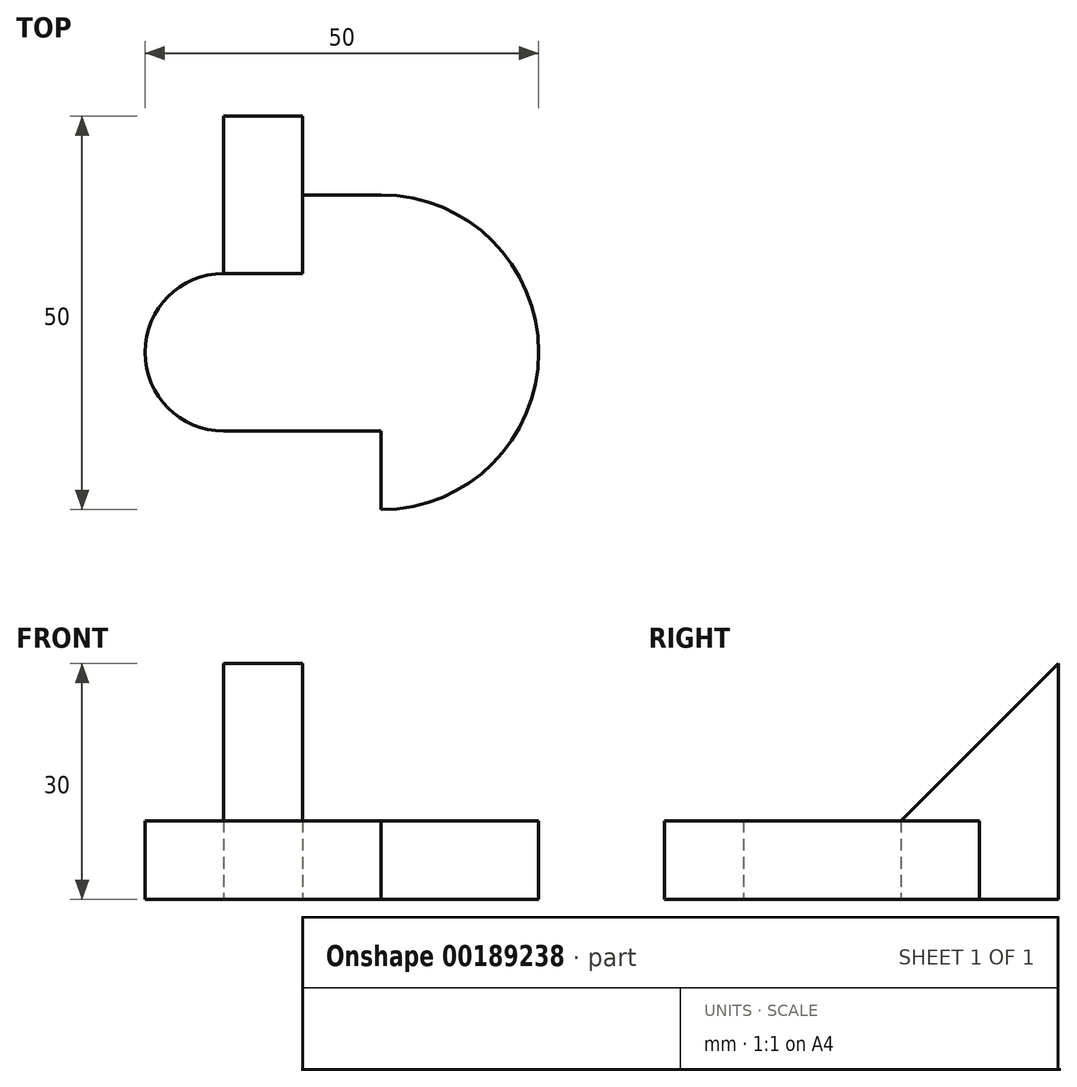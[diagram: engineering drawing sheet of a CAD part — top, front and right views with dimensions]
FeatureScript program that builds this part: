
annotation { "Feature Type Name" : "Feature", "Feature Type Description" : "" }
export const myFeature = defineFeature(function(context is Context, id is Id, definition is map)
    precondition{}
    {
        {
            var Q0;
            Q0=qCreatedBy(makeId("Top.planeOp"),FACE);
            var sketch = newSketch(context, id + "F0", { "sketchPlane" : qUnion([Q0])});
            skArc(sketch, "E0", {"start": v(0, 10) * mm, "mid": v(-10, 0) * mm, "end": v(0, -10) * mm});
            skLineSegment(sketch, "E1", {"start": v(0, -10) * mm, "end": v(20, -10) * mm});
            skLineSegment(sketch, "E2", {"start": v(20, -10) * mm, "end": v(20, -20) * mm});
            skLineSegment(sketch, "E3", {"start": v(0, 10) * mm, "end": v(10, 10) * mm});
            skLineSegment(sketch, "E4", {"start": v(10, 10) * mm, "end": v(10, 20) * mm});
            skLineSegment(sketch, "E5", {"start": v(10, 20) * mm, "end": v(20, 20) * mm});
            skArc(sketch, "E6.trimOffspring", {"start": v(20, -20) * mm, "mid": v(40, 0) * mm, "end": v(20, 20) * mm});
            skSolve(sketch);
        }
        {
            var Q0;
            Q0=makeQuery(id+"F0.imprint","IMPRINT",FACE,{"disambiguationData":[TD([[makeQuery(id+"F0.imprint","IMPRINT",EDGE,{"derivedFrom":sQuery(id+"F0.wireOp",EDGE,"E0")}),1.0]])]});
            extrude(context, id + "F1", {"entities" : qUnion([Q0]), "depth" : 10 * mm});
        }
        {
            var Q0;
            Q0=makeQuery(id+"F1.opExtrude","SWEPT_FACE",FACE,{"disambiguationData":[OSD([sQuery(id+"F0.wireOp",EDGE,"E4")])]});
            var sketch = newSketch(context, id + "F2", { "sketchPlane" : qUnion([Q0])});
            skLineSegment(sketch, "E7", {"start": v(-20, 0) * mm, "end": v(-30, 0) * mm});
            skLineSegment(sketch, "E8", {"start": v(-30, 0) * mm, "end": v(-30, 30) * mm});
            skLineSegment(sketch, "E9", {"start": v(-30, 30) * mm, "end": v(-10, 10) * mm});
            skLineSegment(sketch, "E10.0", {"start": v(-10, 0) * mm, "end": v(-20, 0) * mm});
            skLineSegment(sketch, "E11.0", {"start": v(-10, 10) * mm, "end": v(-10, 0) * mm});
            skSolve(sketch);
        }
        {
            var Q0;
            Q0=makeQuery(id+"F2.imprint","IMPRINT",FACE,{"disambiguationData":[TD([[makeQuery(id+"F2.imprint","IMPRINT",EDGE,{"derivedFrom":sQuery(id+"F2.wireOp",EDGE,"E7")}),-1.0]])]});
            var Q1;
            Q1=makeQuery(id+"F2.imprint","IMPRINT",FACE,{"disambiguationData":[TD([[makeQuery(id+"F2.imprint","IMPRINT",EDGE,{"derivedFrom":sQuery(id+"F2.wireOp",EDGE,"E10.0")}),-1.0]])]});
            extrude(context, id + "F3", {"entities" : qUnion([Q0, Q1]), "operationType" : NewBodyOperationType.ADD, "depth" : 10 * mm});
        }
    });
